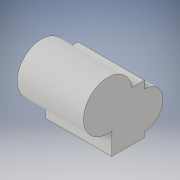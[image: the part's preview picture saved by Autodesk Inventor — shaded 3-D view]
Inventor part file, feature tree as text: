
AUTODESK INVENTOR PART (.ipt)
format: ipt  version: 2017 (Build 210142000, 142)  size: 97,792 bytes
history: native  units: in
note: dims shown in document units (in); Inventor stores cm internally (conversion verified against a paired STEP export)
features: extrude x1, sketch x1
ambient origin geometry x8: Origin, YZ Plane, XZ Plane, XY Plane, X Axis, Y Axis, Z Axis, Center Point
bodies: Solid1 (feature_tree)
feature tree (2):
  extrude  "Extrusion1"  [1 undecoded]
  sketch  "Sketch1"  dims[d0=1.0in d1=0.0in]
note: 1 required parameter value undecoded (feature->parameter linkage not recoverable at this tier; creation-order binding heuristic only, values carry confidence <= 0.55)
